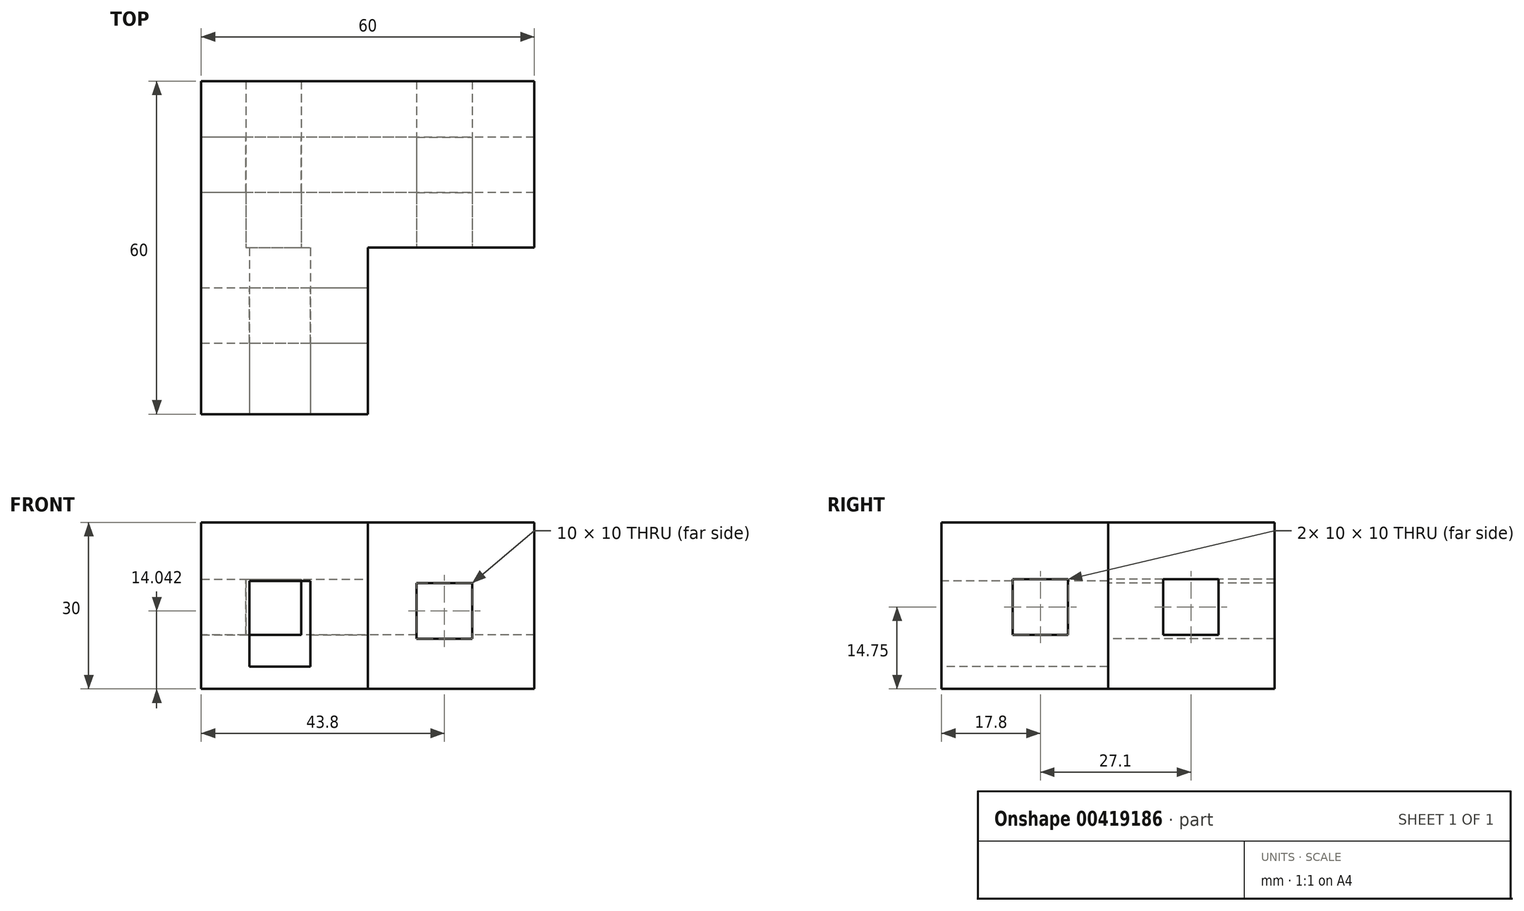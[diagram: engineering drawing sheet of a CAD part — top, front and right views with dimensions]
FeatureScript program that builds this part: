
annotation { "Feature Type Name" : "Feature", "Feature Type Description" : "" }
export const myFeature = defineFeature(function(context is Context, id is Id, definition is map)
    precondition{}
    {
        {
            var Q0;
            Q0=qCreatedBy(makeId("Top.planeOp"),FACE);
            var sketch = newSketch(context, id + "F0", { "sketchPlane" : qUnion([Q0])});
            skLineSegment(sketch, "E0.top", {"start": v(0, 30) * mm, "end": v(-30, 30) * mm});
            skLineSegment(sketch, "E0.right", {"start": v(-30, 0) * mm, "end": v(-30, 30) * mm});
            skLineSegment(sketch, "E1.bottom", {"start": v(0, 30) * mm, "end": v(30, 30) * mm});
            skLineSegment(sketch, "E1.top", {"start": v(0, 0) * mm, "end": v(30, 0) * mm});
            skLineSegment(sketch, "E1.right", {"start": v(30, 30) * mm, "end": v(30, 0) * mm});
            skLineSegment(sketch, "E2.top", {"start": v(-30, -30) * mm, "end": v(0, -30) * mm});
            skLineSegment(sketch, "E2.left", {"start": v(-30, 0) * mm, "end": v(-30, -30) * mm});
            skLineSegment(sketch, "E2.right", {"start": v(0, 0) * mm, "end": v(0, -30) * mm});
            skSolve(sketch);
        }
        {
            var Q0;
            Q0 = qSketchRegion(id + "F0", true);
            extrude(context, id + "F1", {"entities" : qUnion([Q0]), "depth" : 30 * mm});
        }
        {
            var Q0;
            Q0=qCreatedBy(makeId("Front.planeOp"),FACE);
            var sketch = newSketch(context, id + "F2", { "sketchPlane" : qUnion([Q0])});
            skLineSegment(sketch, "E3.bottom", {"start": v(8.8, 19.04) * mm, "end": v(18.8, 19.04) * mm});
            skLineSegment(sketch, "E3.top", {"start": v(8.8, 9.04) * mm, "end": v(18.8, 9.04) * mm});
            skLineSegment(sketch, "E3.left", {"start": v(8.8, 19.04) * mm, "end": v(8.8, 9.04) * mm});
            skLineSegment(sketch, "E3.right", {"start": v(18.8, 19.04) * mm, "end": v(18.8, 9.04) * mm});
            skSolve(sketch);
        }
        {
            var Q0;
            Q0 = qSketchRegion(id + "F2", true);
            extrude(context, id + "F3", {"entities" : qUnion([Q0]), "operationType" : NewBodyOperationType.REMOVE, "oppositeDirection" : true, "depth" : 30 * mm});
        }
        {
            var Q0;
            Q0=makeQuery(id+"F1.opExtrude","SWEPT_FACE",FACE,{"disambiguationData":[OSD([sQuery(id+"F0.wireOp",EDGE,"E2.right")])]});
            var sketch = newSketch(context, id + "F4", { "sketchPlane" : qUnion([Q0])});
            skLineSegment(sketch, "E4.bottom", {"start": v(-17.2, 19.75) * mm, "end": v(-7.2, 19.75) * mm});
            skLineSegment(sketch, "E4.top", {"start": v(-17.2, 9.75) * mm, "end": v(-7.2, 9.75) * mm});
            skLineSegment(sketch, "E4.left", {"start": v(-17.2, 19.75) * mm, "end": v(-17.2, 9.75) * mm});
            skLineSegment(sketch, "E4.right", {"start": v(-7.2, 19.75) * mm, "end": v(-7.2, 9.75) * mm});
            skSolve(sketch);
        }
        {
            var Q0;
            Q0 = qSketchRegion(id + "F4", true);
            extrude(context, id + "F5", {"entities" : qUnion([Q0]), "operationType" : NewBodyOperationType.REMOVE, "oppositeDirection" : true, "depth" : 30 * mm});
        }
        {
            var Q0;
            Q0=makeQuery(id+"F1.opExtrude","SWEPT_FACE",FACE,{"disambiguationData":[OSD([sQuery(id+"F0.wireOp",EDGE,"E0.right"),sQuery(id+"F0.wireOp",EDGE,"E2.left")])]});
            var sketch = newSketch(context, id + "F6", { "sketchPlane" : qUnion([Q0])});
            skLineSegment(sketch, "E5.bottom", {"start": v(-19.9, 19.75) * mm, "end": v(-9.9, 19.75) * mm});
            skLineSegment(sketch, "E5.top", {"start": v(-19.9, 9.75) * mm, "end": v(-9.9, 9.75) * mm});
            skLineSegment(sketch, "E5.left", {"start": v(-19.9, 19.75) * mm, "end": v(-19.9, 9.75) * mm});
            skLineSegment(sketch, "E5.right", {"start": v(-9.9, 19.75) * mm, "end": v(-9.9, 9.75) * mm});
            skPoint(sketch, "E6", {"position": v(12.2, 9.75) * mm});
            skSolve(sketch);
        }
        {
            var Q0;
            Q0=makeQuery(id+"F6.imprint","IMPRINT",FACE,{"disambiguationData":[TD([[makeQuery(id+"F6.imprint","IMPRINT",EDGE,{"derivedFrom":sQuery(id+"F6.wireOp",EDGE,"E5.bottom")}),-1.0]])]});
            extrude(context, id + "F7", {"entities" : qUnion([Q0]), "operationType" : NewBodyOperationType.REMOVE, "oppositeDirection" : true, "depth" : 60 * mm});
        }
        {
            var Q0;
            Q0=qCreatedBy(makeId("Front.planeOp"),FACE);
            var sketch = newSketch(context, id + "F8", { "sketchPlane" : qUnion([Q0])});
            skLineSegment(sketch, "E7.bottom", {"start": v(-21.98, 19.74) * mm, "end": v(-11.98, 19.74) * mm});
            skLineSegment(sketch, "E7.top", {"start": v(-21.98, 9.74) * mm, "end": v(-11.98, 9.74) * mm});
            skLineSegment(sketch, "E7.left", {"start": v(-21.98, 19.74) * mm, "end": v(-21.98, 9.74) * mm});
            skLineSegment(sketch, "E7.right", {"start": v(-11.98, 19.74) * mm, "end": v(-11.98, 9.74) * mm});
            skSolve(sketch);
        }
        {
            var Q0;
            Q0 = qSketchRegion(id + "F8", true);
            extrude(context, id + "F9", {"entities" : qUnion([Q0]), "operationType" : NewBodyOperationType.REMOVE, "oppositeDirection" : true, "depth" : 60 * mm});
        }
        {
            var Q0;
            Q0=makeQuery(id+"F1.opExtrude","SWEPT_FACE",FACE,{"disambiguationData":[OSD([sQuery(id+"F0.wireOp",EDGE,"E2.top")])]});
            var sketch = newSketch(context, id + "F10", { "sketchPlane" : qUnion([Q0])});
            skLineSegment(sketch, "E8.bottom", {"start": v(-21.3, 19.46) * mm, "end": v(-10.35, 19.46) * mm});
            skLineSegment(sketch, "E8.top", {"start": v(-21.3, 4.02) * mm, "end": v(-10.35, 4.02) * mm});
            skLineSegment(sketch, "E8.left", {"start": v(-21.3, 19.46) * mm, "end": v(-21.3, 4.02) * mm});
            skLineSegment(sketch, "E8.right", {"start": v(-10.35, 19.46) * mm, "end": v(-10.35, 4.02) * mm});
            skSolve(sketch);
        }
        {
            var Q0;
            Q0=makeQuery(id+"F10.imprint","IMPRINT",FACE,{"disambiguationData":[TD([[makeQuery(id+"F10.imprint","IMPRINT",EDGE,{"derivedFrom":sQuery(id+"F10.wireOp",EDGE,"E8.bottom")}),-1.0]])]});
            extrude(context, id + "F11", {"entities" : qUnion([Q0]), "operationType" : NewBodyOperationType.REMOVE, "oppositeDirection" : true, "depth" : 30 * mm});
        }
        {
            var Q0;
            Q0=makeQuery(id+"F1.opExtrude","SWEPT_BODY",BODY,{"disambiguationData":[OSD([sQuery(id+"F0.wireOp",EDGE,"E0.top"),sQuery(id+"F0.wireOp",EDGE,"E0.right"),sQuery(id+"F0.wireOp",EDGE,"E1.bottom"),sQuery(id+"F0.wireOp",EDGE,"E1.top"),sQuery(id+"F0.wireOp",EDGE,"E1.right"),sQuery(id+"F0.wireOp",EDGE,"E2.top"),sQuery(id+"F0.wireOp",EDGE,"E2.left"),sQuery(id+"F0.wireOp",EDGE,"E2.right")])]});
            transform(context, id + "F12", {"entities" : qUnion([Q0]), "transformType" : TransformType.TRANSLATION_3D, "dx" : 0 * mm, "dy" : 0 * mm, "dz" : 0 * mm, "makeCopy" : true});
        }
        {
            var Q0;
            Q0=makeQuery(id+"F12.opPattern","COPY",BODY,{"derivedFrom":makeQuery(id+"F1.opExtrude","SWEPT_BODY",BODY,{"disambiguationData":[OSD([sQuery(id+"F0.wireOp",EDGE,"E0.top"),sQuery(id+"F0.wireOp",EDGE,"E0.right"),sQuery(id+"F0.wireOp",EDGE,"E1.bottom"),sQuery(id+"F0.wireOp",EDGE,"E1.top"),sQuery(id+"F0.wireOp",EDGE,"E1.right"),sQuery(id+"F0.wireOp",EDGE,"E2.top"),sQuery(id+"F0.wireOp",EDGE,"E2.left"),sQuery(id+"F0.wireOp",EDGE,"E2.right")])]}),"instanceName":"1"});
            deleteBodies(context, id + "F13", {"entities" : qUnion([Q0])});
        }
    });
